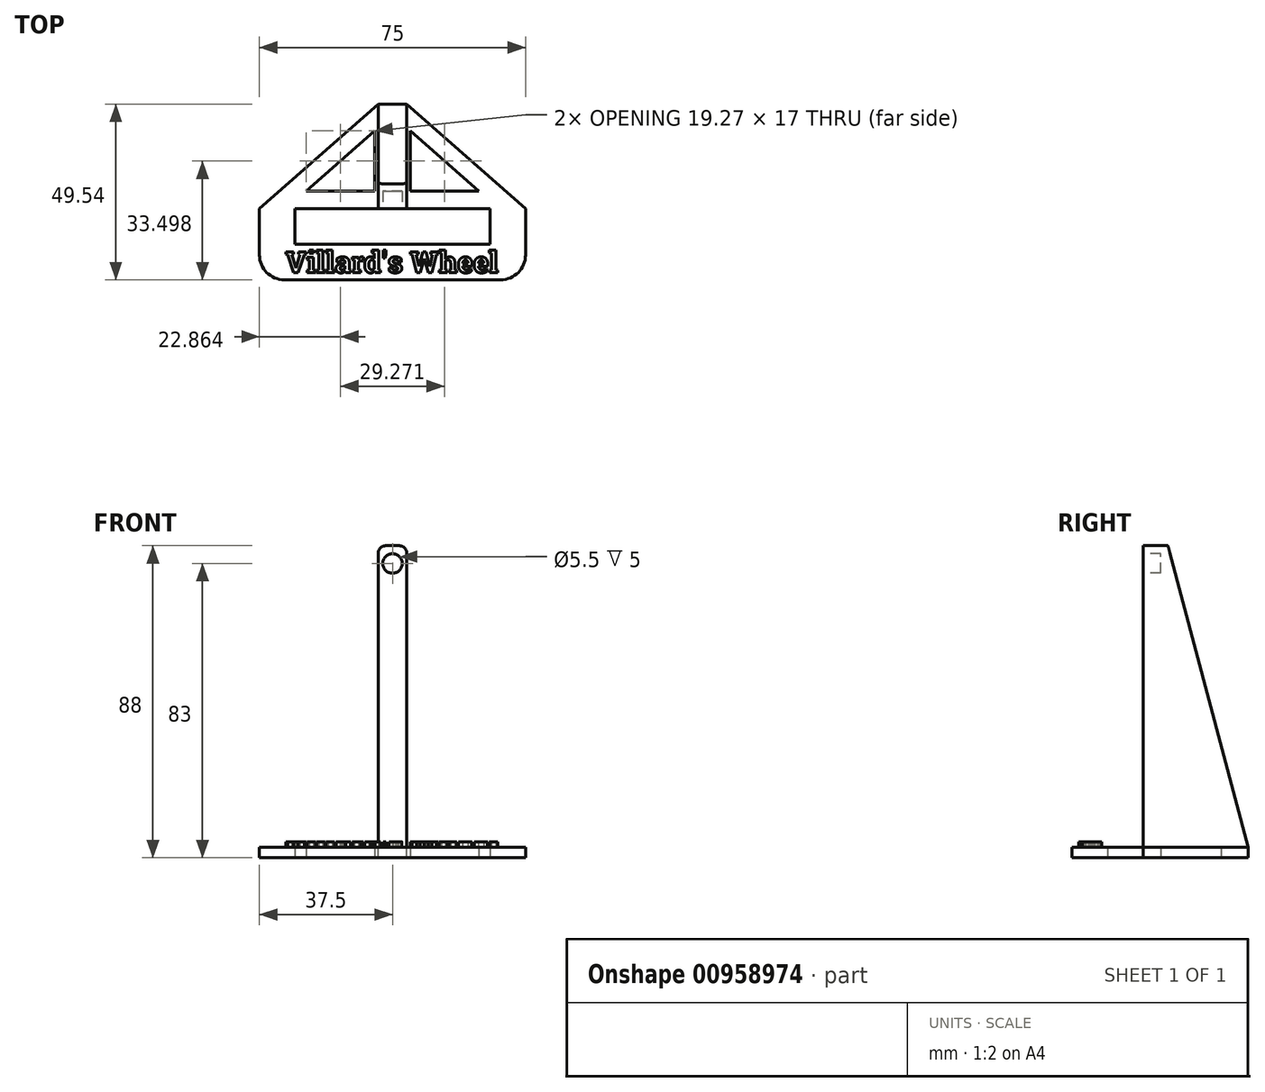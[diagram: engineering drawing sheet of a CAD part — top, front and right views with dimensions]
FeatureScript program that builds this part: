
annotation { "Feature Type Name" : "Feature", "Feature Type Description" : "" }
export const myFeature = defineFeature(function(context is Context, id is Id, definition is map)
    precondition{}
    {
        {
            var Q0;
            Q0=qCreatedBy(makeId("Top.planeOp"),FACE);
            var sketch = newSketch(context, id + "F0", { "sketchPlane" : qUnion([Q0])});
            skLineSegment(sketch, "E0.bottom", {"start": v(10, 0) * mm, "end": v(65, 0) * mm});
            skLineSegment(sketch, "E0.top", {"start": v(0, -20) * mm, "end": v(75, -20) * mm});
            skLineSegment(sketch, "E0.left", {"start": v(0, 0) * mm, "end": v(0, -20) * mm});
            skLineSegment(sketch, "E0.right", {"start": v(75, 0) * mm, "end": v(75, -20) * mm});
            skLineSegment(sketch, "E1.top", {"start": v(10, -10) * mm, "end": v(65, -10) * mm});
            skLineSegment(sketch, "E1.left", {"start": v(10, 0) * mm, "end": v(10, -10) * mm});
            skLineSegment(sketch, "E1.right", {"start": v(65, 0) * mm, "end": v(65, -10) * mm});
            skLineSegment(sketch, "E2", {"start": v(0, 0) * mm, "end": v(37.5, 33.07) * mm});
            skPoint(sketch, "E2.endSnap0", {"position": v(37.5, -10) * mm});
            skLineSegment(sketch, "E3", {"start": v(37.5, 33.07) * mm, "end": v(75, 0) * mm});
            skLineSegment(sketch, "E4", {"start": v(32.5, 22) * mm, "end": v(13.23, 5) * mm});
            skLineSegment(sketch, "E5", {"start": v(13.23, 5) * mm, "end": v(32.5, 5) * mm});
            skLineSegment(sketch, "E6", {"start": v(32.5, 5) * mm, "end": v(32.5, 22) * mm});
            skLineSegment(sketch, "E7", {"start": v(42.5, 22) * mm, "end": v(42.5, 5) * mm});
            skLineSegment(sketch, "E8", {"start": v(42.5, 22) * mm, "end": v(61.77, 5) * mm});
            skLineSegment(sketch, "E9", {"start": v(61.77, 5) * mm, "end": v(42.5, 5) * mm});
            skSolve(sketch);
        }
        {
            var Q0;
            Q0 = qSketchRegion(id + "F0", true);
            extrude(context, id + "F1", {"entities" : qUnion([Q0]), "depth" : 3 * mm, "offsetDistance" : 25 * mm});
        }
        {
            var Q0;
            Q0=makeQuery(id+"F1.opExtrude","CAP_FACE",FACE,{"disambiguationData":[OSD([sQuery(id+"F0.wireOp",EDGE,"E0.top"),sQuery(id+"F0.wireOp",EDGE,"E0.left"),sQuery(id+"F0.wireOp",EDGE,"E0.right"),sQuery(id+"F0.wireOp",EDGE,"E0.bottom"),sQuery(id+"F0.wireOp",EDGE,"E1.top"),sQuery(id+"F0.wireOp",EDGE,"E1.left"),sQuery(id+"F0.wireOp",EDGE,"E1.right"),sQuery(id+"F0.wireOp",EDGE,"E2"),sQuery(id+"F0.wireOp",EDGE,"E3"),sQuery(id+"F0.wireOp",EDGE,"E4"),sQuery(id+"F0.wireOp",EDGE,"E5"),sQuery(id+"F0.wireOp",EDGE,"E6"),sQuery(id+"F0.wireOp",EDGE,"E7"),sQuery(id+"F0.wireOp",EDGE,"E8"),sQuery(id+"F0.wireOp",EDGE,"E9")])],"isStart":false});
            var sketch = newSketch(context, id + "F2", { "sketchPlane" : qUnion([Q0])});
            skLineSegment(sketch, "E10.bottom", {"start": v(41.5, 0) * mm, "end": v(33.5, 0) * mm});
            skLineSegment(sketch, "E10.top", {"start": v(41.5, 29.54) * mm, "end": v(33.5, 29.54) * mm});
            skLineSegment(sketch, "E10.left", {"start": v(41.5, 0) * mm, "end": v(41.5, 29.54) * mm});
            skLineSegment(sketch, "E10.right", {"start": v(33.5, 0) * mm, "end": v(33.5, 29.54) * mm});
            skPoint(sketch, "E10.middle", {"position": v(37.5, 14.77) * mm});
            skSolve(sketch);
        }
        {
            var Q0;
            Q0 = qSketchRegion(id + "F2", true);
            extrude(context, id + "F3", {"entities" : qUnion([Q0]), "operationType" : NewBodyOperationType.ADD, "depth" : 85 * mm, "offsetDistance" : 25 * mm});
        }
        {
            var Q0;
            {var subQ0=sQuery(id+"F0.wireOp",EDGE,"E2");var subQ1=sQuery(id+"F2.wireOp",EDGE,"E10.top");var subQ2=sQuery(id+"F0.wireOp",EDGE,"E3");Q0=makeQuery(id+"F3.boolean.opBoolean","SPLIT",FACE,{"disambiguationData":[TD([makeQuery(id+"F3.opExtrude","SWEPT_FACE",FACE,{"disambiguationData":[OSD([subQ1])]})])],"derivedFrom":makeQuery(id+"F1.opExtrude","CAP_FACE",FACE,{"disambiguationData":[OSD([sQuery(id+"F0.wireOp",EDGE,"E0.top"),sQuery(id+"F0.wireOp",EDGE,"E0.left"),sQuery(id+"F0.wireOp",EDGE,"E0.right"),sQuery(id+"F0.wireOp",EDGE,"E0.bottom"),sQuery(id+"F0.wireOp",EDGE,"E1.top"),sQuery(id+"F0.wireOp",EDGE,"E1.left"),sQuery(id+"F0.wireOp",EDGE,"E1.right"),subQ0,subQ2,sQuery(id+"F0.wireOp",EDGE,"E4"),sQuery(id+"F0.wireOp",EDGE,"E5"),sQuery(id+"F0.wireOp",EDGE,"E6"),sQuery(id+"F0.wireOp",EDGE,"E7"),sQuery(id+"F0.wireOp",EDGE,"E8"),sQuery(id+"F0.wireOp",EDGE,"E9")])],"isStart":false})});}
            extrude(context, id + "F4", {"entities" : qUnion([Q0]), "operationType" : NewBodyOperationType.REMOVE, "endBound" : BoundingType.UP_TO_NEXT, "oppositeDirection" : true, "depth" : 25 * mm, "offsetDistance" : 25 * mm});
        }
        {
            var Q0;
            Q0=makeQuery(id+"F3.boolean.opBoolean","MERGE",FACE,{"derivedFrom":[makeQuery(id+"F1.opExtrude","SWEPT_FACE",FACE,{"disambiguationData":[OSD([sQuery(id+"F0.wireOp",EDGE,"E0.bottom")])]}),makeQuery(id+"F3.opExtrude","SWEPT_FACE",FACE,{"disambiguationData":[OSD([sQuery(id+"F2.wireOp",EDGE,"E10.bottom")])]})]});
            var sketch = newSketch(context, id + "F5", { "sketchPlane" : qUnion([Q0])});
            skPoint(sketch, "E11.0", {"position": v(37.5, 88) * mm});
            skLineSegment(sketch, "E12", {"start": v(37.5, 88) * mm, "end": v(37.5, 83) * mm, "construction": true});
            skCircle(sketch, "E13", {"center": v(37.5, 83) * mm, "radius": 2.75 * mm});
            skSolve(sketch);
        }
        {
            var Q0;
            Q0 = qSketchRegion(id + "F5", true);
            extrude(context, id + "F6", {"entities" : qUnion([Q0]), "operationType" : NewBodyOperationType.REMOVE, "oppositeDirection" : true, "depth" : 5 * mm, "offsetDistance" : 25 * mm});
        }
        {
            var Q0;
            Q0=makeQuery(id+"F3.opExtrude","SWEPT_FACE",FACE,{"disambiguationData":[OSD([sQuery(id+"F2.wireOp",EDGE,"E10.right")])]});
            var sketch = newSketch(context, id + "F7", { "sketchPlane" : qUnion([Q0])});
            skLineSegment(sketch, "E14", {"start": v(-7, 88) * mm, "end": v(-29.54, 3) * mm});
            skLineSegment(sketch, "E15.0", {"start": v(-29.54, 88) * mm, "end": v(-29.54, 3) * mm});
            skLineSegment(sketch, "E16.0", {"start": v(-7, 88) * mm, "end": v(-29.54, 88) * mm});
            skPoint(sketch, "E17.orphan", {"position": v(0, 88) * mm});
            skSolve(sketch);
        }
        {
            var Q0;
            Q0 = qSketchRegion(id + "F7", true);
            extrude(context, id + "F8", {"entities" : qUnion([Q0]), "operationType" : NewBodyOperationType.REMOVE, "endBound" : BoundingType.UP_TO_NEXT, "oppositeDirection" : true, "depth" : 25 * mm, "offsetDistance" : 25 * mm});
        }
        {
            var Q0;
            Q0=makeQuery(id+"F8.boolean.opBoolean","COPY",EDGE,{"derivedFrom":makeQuery(id+"F8.opExtrude","CAP_EDGE",EDGE,{"disambiguationData":[OSD([sQuery(id+"F7.wireOp",EDGE,"E14")])],"isStart":true})});
            var Q1;
            Q1=makeQuery(id+"F8.boolean.opBoolean","COPY",EDGE,{"derivedFrom":makeQuery(id+"F8.opExtrude","TWEAK_EDGE",EDGE,{"derivedFrom":[makeQuery(id+"F3.opExtrude","SWEPT_FACE",FACE,{"disambiguationData":[OSD([sQuery(id+"F2.wireOp",EDGE,"E10.left")])]}),makeQuery(id+"F7.imprint","IMPRINT",EDGE,{"derivedFrom":sQuery(id+"F7.wireOp",EDGE,"E14")})]})});
            var Q2;
            Q2=makeQuery(id+"F8.boolean.opBoolean","COPY",EDGE,{"derivedFrom":makeQuery(id+"F8.opExtrude","SWEPT_EDGE",EDGE,{"disambiguationData":[OSD([sQuery(id+"F2.wireOp",EDGE,"E10.right"),sQuery(id+"F7.wireOp",EDGE,"E14"),sQuery(id+"F7.wireOp",EDGE,"E16.0")])]})});
            var Q3;
            Q3=makeQuery(id+"F3.opExtrude","CAP_EDGE",EDGE,{"disambiguationData":[OSD([sQuery(id+"F2.wireOp",EDGE,"E10.right")])],"isStart":false});
            var Q4;
            Q4=makeQuery(id+"F3.opExtrude","CAP_EDGE",EDGE,{"disambiguationData":[OSD([sQuery(id+"F2.wireOp",EDGE,"E10.left")])],"isStart":false});
            fillet(context, id + "F9", {"entities" : qUnion([Q0, Q1, Q2, Q3, Q4]), "radius" : 2 * mm, "tangentPropagation" : true, "allowEdgeOverflow" : false});
        }
        {
            var Q0;
            Q0=makeQuery(id+"F1.opExtrude","SWEPT_EDGE",EDGE,{"disambiguationData":[OSD([sQuery(id+"F0.wireOp",EDGE,"E0.top"),sQuery(id+"F0.wireOp",EDGE,"E0.left")])]});
            var Q1;
            Q1=makeQuery(id+"F1.opExtrude","SWEPT_EDGE",EDGE,{"disambiguationData":[OSD([sQuery(id+"F0.wireOp",EDGE,"E0.top"),sQuery(id+"F0.wireOp",EDGE,"E0.right")])]});
            fillet(context, id + "F10", {"entities" : qUnion([Q0, Q1]), "radius" : 7 * mm, "tangentPropagation" : true, "allowEdgeOverflow" : false});
        }
        {
            var Q0;
            {var subQ0=sQuery(id+"F0.wireOp",EDGE,"E3");var subQ1=sQuery(id+"F0.wireOp",EDGE,"E2");var subQ2=sQuery(id+"F0.wireOp",EDGE,"E1.right");var subQ3=sQuery(id+"F0.wireOp",EDGE,"E1.left");var subQ4=sQuery(id+"F0.wireOp",EDGE,"E1.top");var subQ5=sQuery(id+"F0.wireOp",EDGE,"E0.bottom");var subQ6=sQuery(id+"F0.wireOp",EDGE,"E0.top");var subQ7=sQuery(id+"F0.wireOp",EDGE,"E9");var subQ8=sQuery(id+"F0.wireOp",EDGE,"E8");var subQ9=sQuery(id+"F0.wireOp",EDGE,"E7");var subQ10=sQuery(id+"F0.wireOp",EDGE,"E6");var subQ11=sQuery(id+"F0.wireOp",EDGE,"E5");var subQ12=sQuery(id+"F0.wireOp",EDGE,"E4");var subQ13=sQuery(id+"F0.wireOp",EDGE,"E0.right");var subQ14=sQuery(id+"F0.wireOp",EDGE,"E0.left");var subQ15=makeQuery(id+"F1.opExtrude","CAP_FACE",FACE,{"disambiguationData":[OSD([subQ6,subQ14,subQ13,subQ5,subQ4,subQ3,subQ2,subQ1,subQ0,subQ12,subQ11,subQ10,subQ9,subQ8,subQ7])],"isStart":false});Q0=makeQuery(id+"F3.boolean.opBoolean","SPLIT",FACE,{"disambiguationData":[TD([makeQuery(id+"F1.opExtrude","SWEPT_FACE",FACE,{"disambiguationData":[OSD([subQ6])]}),subQ15,makeQuery(id+"F1.opExtrude","SWEPT_FACE",FACE,{"disambiguationData":[OSD([subQ14])]}),makeQuery(id+"F1.opExtrude","SWEPT_FACE",FACE,{"disambiguationData":[OSD([subQ13])]}),makeQuery(id+"F1.opExtrude","SWEPT_FACE",FACE,{"disambiguationData":[OSD([subQ5])]}),makeQuery(id+"F1.opExtrude","SWEPT_FACE",FACE,{"disambiguationData":[OSD([subQ4])]}),makeQuery(id+"F1.opExtrude","SWEPT_FACE",FACE,{"disambiguationData":[OSD([subQ3])]}),makeQuery(id+"F1.opExtrude","SWEPT_FACE",FACE,{"disambiguationData":[OSD([subQ2])]}),makeQuery(id+"F1.opExtrude","SWEPT_FACE",FACE,{"disambiguationData":[OSD([subQ1])]}),makeQuery(id+"F1.opExtrude","SWEPT_FACE",FACE,{"disambiguationData":[OSD([subQ0])]}),makeQuery(id+"F1.opExtrude","SWEPT_FACE",FACE,{"disambiguationData":[OSD([subQ12])]}),makeQuery(id+"F1.opExtrude","SWEPT_FACE",FACE,{"disambiguationData":[OSD([subQ11])]}),makeQuery(id+"F1.opExtrude","SWEPT_FACE",FACE,{"disambiguationData":[OSD([subQ10])]}),makeQuery(id+"F1.opExtrude","SWEPT_FACE",FACE,{"disambiguationData":[OSD([subQ9])]}),makeQuery(id+"F1.opExtrude","SWEPT_FACE",FACE,{"disambiguationData":[OSD([subQ8])]}),makeQuery(id+"F1.opExtrude","SWEPT_FACE",FACE,{"disambiguationData":[OSD([subQ7])]}),makeQuery(id+"F3.opExtrude","SWEPT_FACE",FACE,{"disambiguationData":[OSD([sQuery(id+"F2.wireOp",EDGE,"E10.bottom")])]}),makeQuery(id+"F3.opExtrude","SWEPT_FACE",FACE,{"disambiguationData":[OSD([sQuery(id+"F2.wireOp",EDGE,"E10.top")])]}),makeQuery(id+"F3.opExtrude","SWEPT_FACE",FACE,{"disambiguationData":[OSD([sQuery(id+"F2.wireOp",EDGE,"E10.left")])]}),makeQuery(id+"F3.opExtrude","SWEPT_FACE",FACE,{"disambiguationData":[OSD([sQuery(id+"F2.wireOp",EDGE,"E10.right")])]})])],"derivedFrom":subQ15});}
            var sketch = newSketch(context, id + "F11", { "sketchPlane" : qUnion([Q0])});
            skText(sketch, "E18", { "text": "Villard\'s Wheel", "fontName": "RobotoSlab-Bold.ttf"});
            skLineSegment(sketch, "E19", {"start": v(37.5, -18) * mm, "end": v(37.5, -20) * mm, "construction": true});
            const initialGuessF11  = {"E18": [0.0073, -0.018, 1, 0, 0.006]};
            skSetInitialGuess(sketch, initialGuessF11);
            skSolve(sketch);
        }
        {
            var Q0;
            Q0 = qSketchRegion(id + "F11", true);
            extrude(context, id + "F12", {"entities" : qUnion([Q0]), "operationType" : NewBodyOperationType.ADD, "depth" : 1.5 * mm, "offsetDistance" : 25 * mm});
        }
    });
